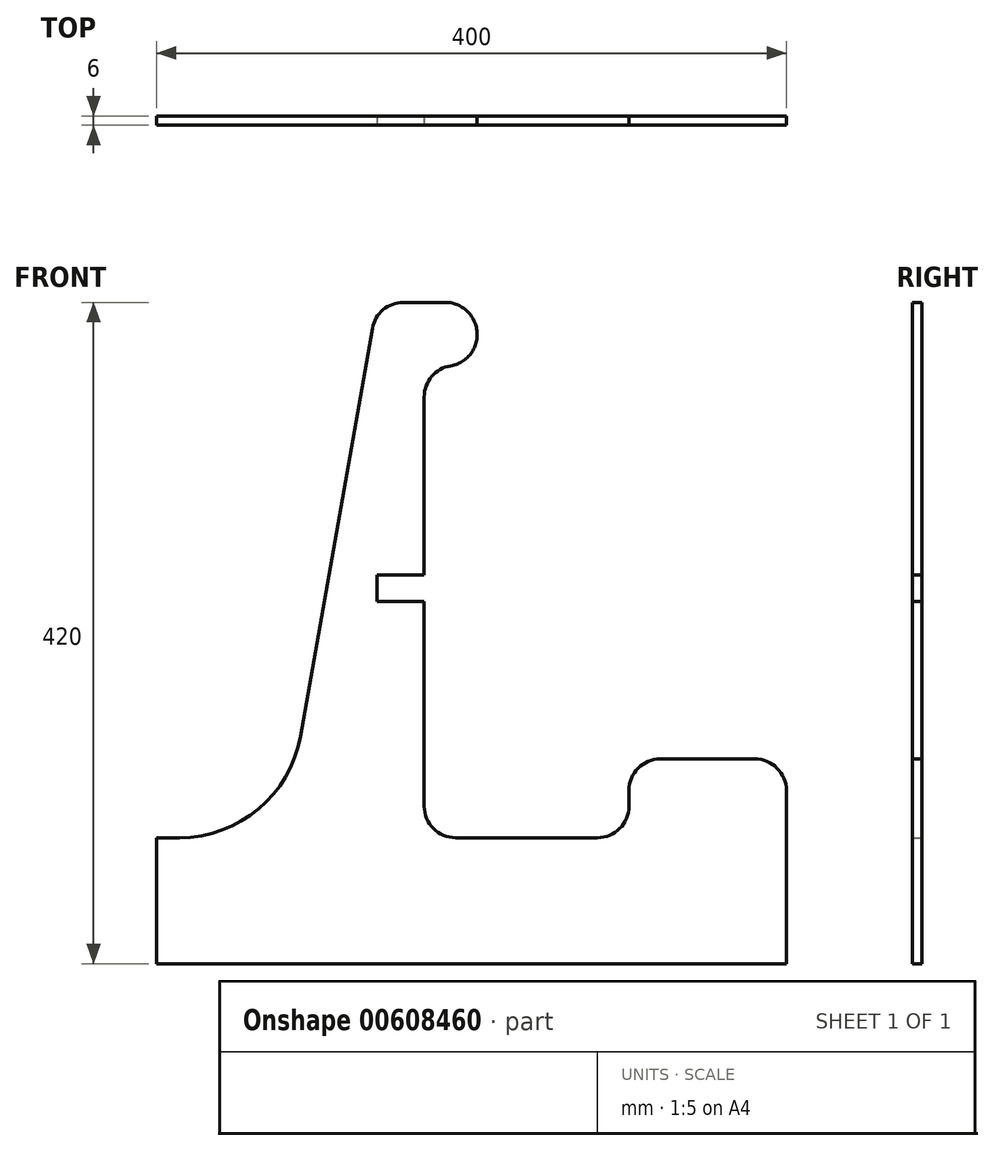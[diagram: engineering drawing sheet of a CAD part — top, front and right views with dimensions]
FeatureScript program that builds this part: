
annotation { "Feature Type Name" : "Feature", "Feature Type Description" : "" }
export const myFeature = defineFeature(function(context is Context, id is Id, definition is map)
    precondition{}
    {
        {
            var Q0;
            Q0=qCreatedBy(makeId("Front.planeOp"),FACE);
            var sketch = newSketch(context, id + "F0", { "sketchPlane" : qUnion([Q0])});
            skLineSegment(sketch, "E0", {"start": v(0, 0) * mm, "end": v(400, 0) * mm});
            skLineSegment(sketch, "E1", {"start": v(400, 0) * mm, "end": v(400, 110) * mm});
            skLineSegment(sketch, "E2", {"start": v(380, 130) * mm, "end": v(320, 130) * mm});
            skLineSegment(sketch, "E3", {"start": v(300, 110) * mm, "end": v(300, 100) * mm});
            skLineSegment(sketch, "E4", {"start": v(280, 80) * mm, "end": v(190, 80) * mm});
            skLineSegment(sketch, "E5", {"start": v(170, 100) * mm, "end": v(170, 360) * mm});
            skLineSegment(sketch, "E6", {"start": v(190, 380) * mm, "end": v(212, 380) * mm});
            skLineSegment(sketch, "E7", {"start": v(212, 380) * mm, "end": v(202.23, 406.84) * mm});
            skLineSegment(sketch, "E8", {"start": v(137.04, 403.47) * mm, "end": v(91.37, 144.46) * mm});
            skLineSegment(sketch, "E9", {"start": v(14.55, 80) * mm, "end": v(0, 80) * mm});
            skLineSegment(sketch, "E10", {"start": v(0, 80) * mm, "end": v(0, 0) * mm});
            skLineSegment(sketch, "E11", {"start": v(156.73, 420) * mm, "end": v(183.44, 420) * mm});
            skPoint(sketch, "E12.visualSharp", {"position": v(80, 80) * mm});
            skArc(sketch, "E12.filletArc", {"start": v(14.55, 80) * mm, "mid": v(64.69, 98.25) * mm, "end": v(91.37, 144.46) * mm});
            skPoint(sketch, "E13.visualSharp", {"position": v(139.95, 420) * mm});
            skArc(sketch, "E13.filletArc", {"start": v(156.73, 420) * mm, "mid": v(143.88, 415.32) * mm, "end": v(137.04, 403.47) * mm});
            skPoint(sketch, "E14.visualSharp", {"position": v(170, 380) * mm});
            skArc(sketch, "E14.filletArc", {"start": v(190, 380) * mm, "mid": v(175.86, 374.14) * mm, "end": v(170, 360) * mm});
            skPoint(sketch, "E15.visualSharp", {"position": v(197.44, 420) * mm});
            skArc(sketch, "E15.filletArc", {"start": v(202.23, 406.84) * mm, "mid": v(194.9, 416.38) * mm, "end": v(183.44, 420) * mm});
            skPoint(sketch, "E16.visualSharp", {"position": v(300, 130) * mm});
            skArc(sketch, "E16.filletArc", {"start": v(320, 130) * mm, "mid": v(305.86, 124.14) * mm, "end": v(300, 110) * mm});
            skPoint(sketch, "E17.visualSharp", {"position": v(400, 130) * mm});
            skArc(sketch, "E17.filletArc", {"start": v(400, 110) * mm, "mid": v(394.14, 124.14) * mm, "end": v(380, 130) * mm});
            skPoint(sketch, "E18.visualSharp", {"position": v(300, 80) * mm});
            skArc(sketch, "E18.filletArc", {"start": v(280, 80) * mm, "mid": v(294.14, 85.86) * mm, "end": v(300, 100) * mm});
            skPoint(sketch, "E19.visualSharp", {"position": v(170, 80) * mm});
            skArc(sketch, "E19.filletArc", {"start": v(170, 100) * mm, "mid": v(175.86, 85.86) * mm, "end": v(190, 80) * mm});
            skSolve(sketch);
        }
        {
            var Q0;
            Q0 = qSketchRegion(id + "F0", true);
            extrude(context, id + "F1", {"entities" : qUnion([Q0]), "depth" : 6 * mm, "offsetDistance" : 25 * mm});
        }
        {
            var Q0;
            Q0=makeQuery(id+"F1.opExtrude","SWEPT_EDGE",EDGE,{"disambiguationData":[OSD([sQuery(id+"F0.wireOp",EDGE,"E6"),sQuery(id+"F0.wireOp",EDGE,"E7")])]});
            fillet(context, id + "F2", {"entities" : qUnion([Q0]), "radius" : 20 * mm, "tangentPropagation" : true, "allowEdgeOverflow" : false});
        }
        {
            var Q0;
            Q0=makeQuery(id+"F1.opExtrude","CAP_FACE",FACE,{"disambiguationData":[OSD([sQuery(id+"F0.wireOp",EDGE,"E0"),sQuery(id+"F0.wireOp",EDGE,"E1"),sQuery(id+"F0.wireOp",EDGE,"E2"),sQuery(id+"F0.wireOp",EDGE,"E3"),sQuery(id+"F0.wireOp",EDGE,"E4"),sQuery(id+"F0.wireOp",EDGE,"E5"),sQuery(id+"F0.wireOp",EDGE,"E6"),sQuery(id+"F0.wireOp",EDGE,"E7"),sQuery(id+"F0.wireOp",EDGE,"E8"),sQuery(id+"F0.wireOp",EDGE,"E9"),sQuery(id+"F0.wireOp",EDGE,"E10"),sQuery(id+"F0.wireOp",EDGE,"E11"),sQuery(id+"F0.wireOp",EDGE,"E12.filletArc"),sQuery(id+"F0.wireOp",EDGE,"E13.filletArc"),sQuery(id+"F0.wireOp",EDGE,"E14.filletArc"),sQuery(id+"F0.wireOp",EDGE,"E15.filletArc"),sQuery(id+"F0.wireOp",EDGE,"E16.filletArc"),sQuery(id+"F0.wireOp",EDGE,"E17.filletArc"),sQuery(id+"F0.wireOp",EDGE,"E18.filletArc"),sQuery(id+"F0.wireOp",EDGE,"E19.filletArc")])],"isStart":true});
            var sketch = newSketch(context, id + "F3", { "sketchPlane" : qUnion([Q0])});
            skLineSegment(sketch, "E20.bottom", {"start": v(-400, 0) * mm, "end": v(0, 0) * mm});
            skLineSegment(sketch, "E20.top", {"start": v(-400, 600) * mm, "end": v(0, 600) * mm});
            skLineSegment(sketch, "E20.left", {"start": v(-400, 0) * mm, "end": v(-400, 600) * mm});
            skLineSegment(sketch, "E20.right", {"start": v(0, 0) * mm, "end": v(0, 600) * mm});
            skSolve(sketch);
        }
        {
            var Q0;
            Q0=makeQuery(id+"F1.opExtrude","CAP_FACE",FACE,{"disambiguationData":[OSD([sQuery(id+"F0.wireOp",EDGE,"E0"),sQuery(id+"F0.wireOp",EDGE,"E1"),sQuery(id+"F0.wireOp",EDGE,"E2"),sQuery(id+"F0.wireOp",EDGE,"E3"),sQuery(id+"F0.wireOp",EDGE,"E4"),sQuery(id+"F0.wireOp",EDGE,"E5"),sQuery(id+"F0.wireOp",EDGE,"E6"),sQuery(id+"F0.wireOp",EDGE,"E7"),sQuery(id+"F0.wireOp",EDGE,"E8"),sQuery(id+"F0.wireOp",EDGE,"E9"),sQuery(id+"F0.wireOp",EDGE,"E10"),sQuery(id+"F0.wireOp",EDGE,"E11"),sQuery(id+"F0.wireOp",EDGE,"E12.filletArc"),sQuery(id+"F0.wireOp",EDGE,"E13.filletArc"),sQuery(id+"F0.wireOp",EDGE,"E14.filletArc"),sQuery(id+"F0.wireOp",EDGE,"E15.filletArc"),sQuery(id+"F0.wireOp",EDGE,"E16.filletArc"),sQuery(id+"F0.wireOp",EDGE,"E17.filletArc"),sQuery(id+"F0.wireOp",EDGE,"E18.filletArc"),sQuery(id+"F0.wireOp",EDGE,"E19.filletArc")])],"isStart":false});
            var sketch = newSketch(context, id + "F4", { "sketchPlane" : qUnion([Q0])});
            skPoint(sketch, "E21.oppositeSnap0", {"position": v(170, 230) * mm});
            skLineSegment(sketch, "E21.bottom", {"start": v(140, 247) * mm, "end": v(198.91, 247) * mm});
            skLineSegment(sketch, "E21.top", {"start": v(140, 230) * mm, "end": v(198.91, 230) * mm});
            skLineSegment(sketch, "E21.left", {"start": v(140, 247) * mm, "end": v(140, 230) * mm});
            skLineSegment(sketch, "E21.right", {"start": v(198.91, 247) * mm, "end": v(198.91, 230) * mm});
            skSolve(sketch);
        }
        {
            var Q0;
            Q0 = qSketchRegion(id + "F4", true);
            extrude(context, id + "F5", {"entities" : qUnion([Q0]), "operationType" : NewBodyOperationType.REMOVE, "oppositeDirection" : true, "depth" : 25 * mm, "offsetDistance" : 25 * mm});
        }
    });
